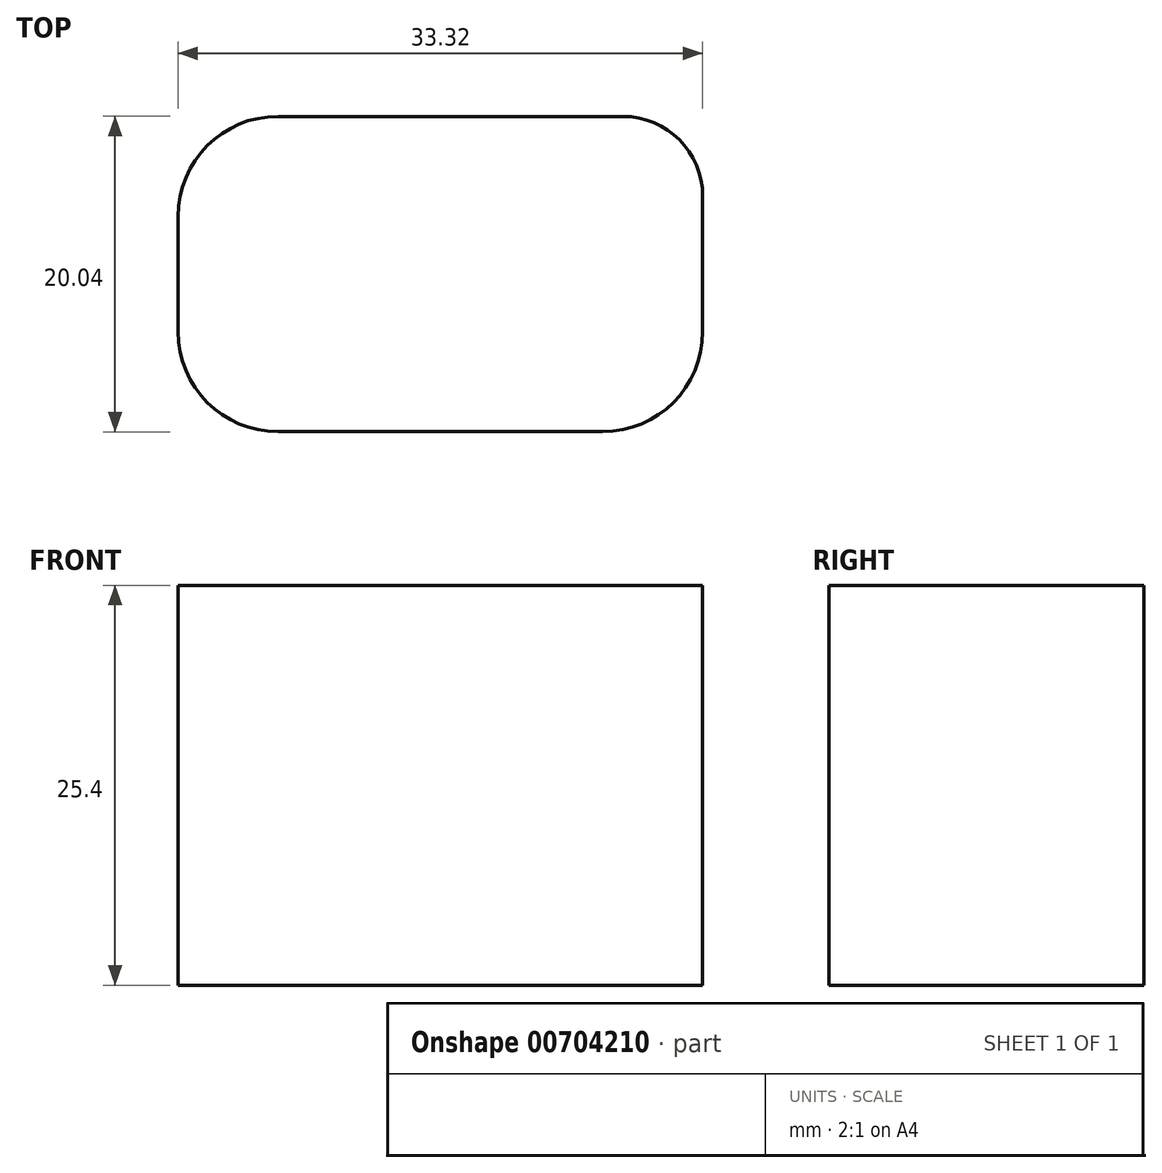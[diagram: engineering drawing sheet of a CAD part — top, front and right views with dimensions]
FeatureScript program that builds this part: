
annotation { "Feature Type Name" : "Feature", "Feature Type Description" : "" }
export const myFeature = defineFeature(function(context is Context, id is Id, definition is map)
    precondition{}
    {
        {
            var Q0;
            Q0=qCreatedBy(makeId("Top.planeOp"),FACE);
            var sketch = newSketch(context, id + "F0", { "sketchPlane" : qUnion([Q0])});
            skLineSegment(sketch, "E0.bottom", {"start": v(33.93, 23.43) * mm, "end": v(54.55, 23.43) * mm});
            skLineSegment(sketch, "E0.top", {"start": v(33.93, 43.47) * mm, "end": v(55.82, 43.47) * mm});
            skLineSegment(sketch, "E0.left", {"start": v(27.58, 29.78) * mm, "end": v(27.58, 37.12) * mm});
            skLineSegment(sketch, "E0.right", {"start": v(60.9, 29.78) * mm, "end": v(60.9, 38.39) * mm});
            skPoint(sketch, "E0.middle", {"position": v(44.24, 33.45) * mm});
            skPoint(sketch, "E1.visualSharp", {"position": v(60.9, 43.47) * mm});
            skArc(sketch, "E1.filletArc", {"start": v(60.9, 38.39) * mm, "mid": v(59.41, 41.98) * mm, "end": v(55.82, 43.47) * mm});
            skPoint(sketch, "E2.visualSharp", {"position": v(60.9, 23.43) * mm});
            skArc(sketch, "E2.filletArc", {"start": v(54.55, 23.43) * mm, "mid": v(59.04, 25.3) * mm, "end": v(60.9, 29.78) * mm});
            skPoint(sketch, "E3.visualSharp", {"position": v(27.58, 23.43) * mm});
            skArc(sketch, "E3.filletArc", {"start": v(27.58, 29.78) * mm, "mid": v(29.44, 25.3) * mm, "end": v(33.93, 23.43) * mm});
            skPoint(sketch, "E4.visualSharp", {"position": v(27.58, 43.47) * mm});
            skArc(sketch, "E4.filletArc", {"start": v(33.93, 43.47) * mm, "mid": v(29.44, 41.6) * mm, "end": v(27.58, 37.12) * mm});
            skSolve(sketch);
        }
        {
            var Q0;
            Q0 = qSketchRegion(id + "F0", true);
            extrude(context, id + "F1", {"entities" : qUnion([Q0]), "depth" : 25.4 * mm, "offsetDistance" : 25.4 * mm});
        }
    });
